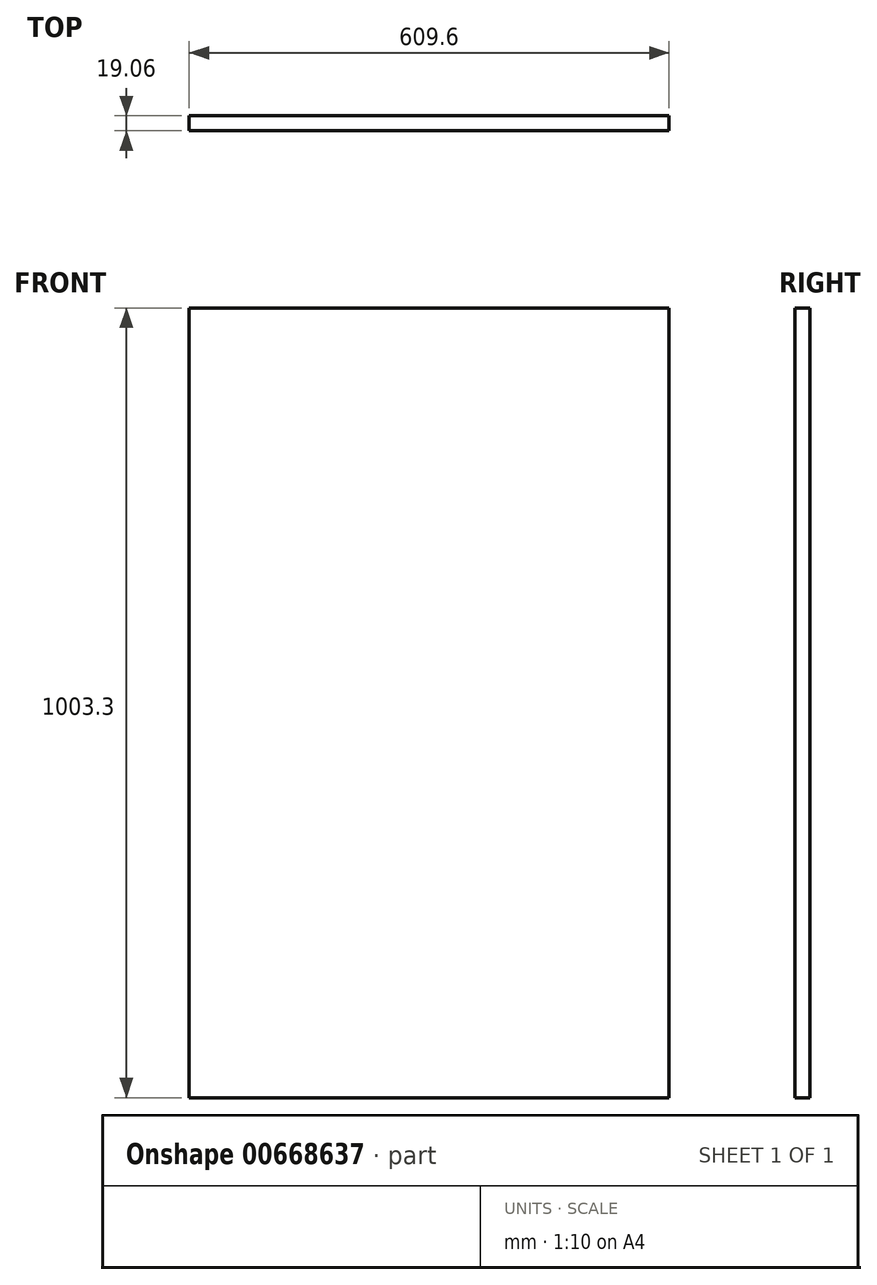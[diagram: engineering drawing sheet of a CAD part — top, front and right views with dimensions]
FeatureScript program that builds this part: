
annotation { "Feature Type Name" : "Feature", "Feature Type Description" : "" }
export const myFeature = defineFeature(function(context is Context, id is Id, definition is map)
    precondition{}
    {
        {
            var Q0;
            Q0=qCreatedBy(makeId("Front.planeOp"),FACE);
            var sketch = newSketch(context, id + "F0", { "sketchPlane" : qUnion([Q0])});
            skLineSegment(sketch, "E0.bottom", {"start": v(-304.8, 501.65) * mm, "end": v(304.8, 501.65) * mm});
            skLineSegment(sketch, "E0.top", {"start": v(-304.8, -501.65) * mm, "end": v(304.8, -501.65) * mm});
            skLineSegment(sketch, "E0.left", {"start": v(-304.8, 501.65) * mm, "end": v(-304.8, -501.65) * mm});
            skLineSegment(sketch, "E0.right", {"start": v(304.8, 501.65) * mm, "end": v(304.8, -501.65) * mm});
            skSolve(sketch);
        }
        {
            var Q0;
            Q0 = qSketchRegion(id + "F0", true);
            extrude(context, id + "F1", {"entities" : qUnion([Q0]), "depth" : 19.05 * mm, "offsetDistance" : 25.4 * mm, "symmetric" : true});
        }
    });
